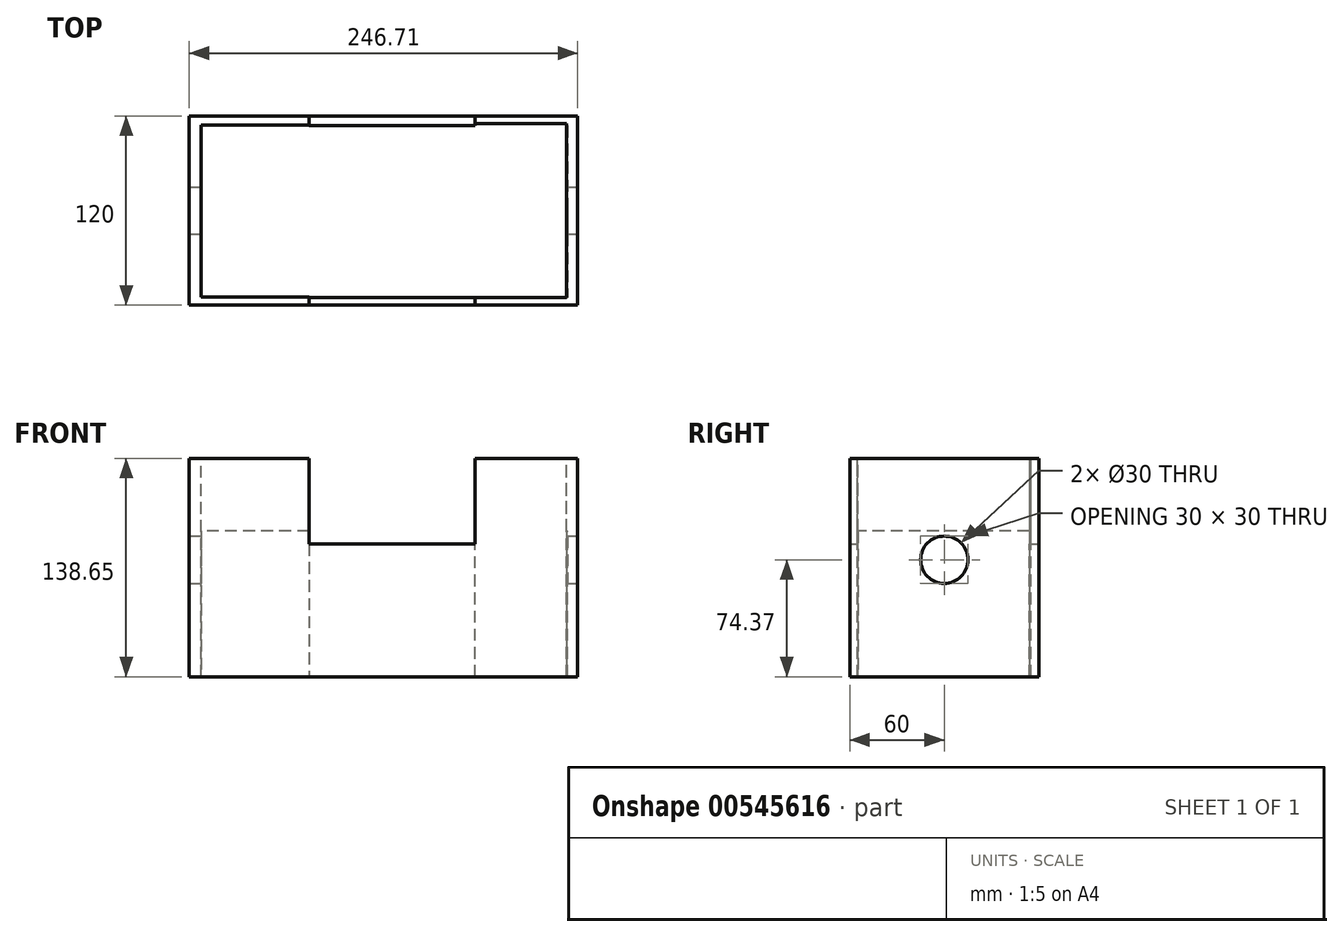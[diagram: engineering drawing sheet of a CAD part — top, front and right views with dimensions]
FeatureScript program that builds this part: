
annotation { "Feature Type Name" : "Feature", "Feature Type Description" : "" }
export const myFeature = defineFeature(function(context is Context, id is Id, definition is map)
    precondition{}
    {
        {
            var Q0;
            Q0=qCreatedBy(makeId("Front.planeOp"),FACE);
            var sketch = newSketch(context, id + "F0", { "sketchPlane" : qUnion([Q0])});
            skLineSegment(sketch, "E0.top", {"start": v(-117.19, -92.62) * mm, "end": v(129.52, -92.62) * mm});
            skLineSegment(sketch, "E0.left", {"start": v(-117.19, 46.03) * mm, "end": v(-117.19, -92.62) * mm});
            skLineSegment(sketch, "E0.right", {"start": v(129.52, 46.03) * mm, "end": v(129.52, -92.62) * mm});
            skLineSegment(sketch, "E1", {"start": v(-117.19, 46.03) * mm, "end": v(-41.02, 46.03) * mm});
            skLineSegment(sketch, "E2", {"start": v(-41.02, 46.03) * mm, "end": v(-41.02, -8.22) * mm});
            skLineSegment(sketch, "E3", {"start": v(-41.02, -8.22) * mm, "end": v(64.28, -8.22) * mm});
            skLineSegment(sketch, "E4", {"start": v(64.28, -8.22) * mm, "end": v(64.28, 46.03) * mm});
            skLineSegment(sketch, "E5", {"start": v(64.28, 46.03) * mm, "end": v(129.52, 46.03) * mm});
            skSolve(sketch);
        }
        {
            var Q0;
            Q0 = qSketchRegion(id + "F0", true);
            extrude(context, id + "F1", {"entities" : qUnion([Q0]), "depth" : 120 * mm, "offsetDistance" : 25 * mm, "symmetric" : true});
        }
        {
            var Q0;
            Q0=qCreatedBy(makeId("Top.planeOp"),FACE);
            var sketch = newSketch(context, id + "F2", { "sketchPlane" : qUnion([Q0])});
            skLineSegment(sketch, "E6.bottom", {"start": v(-109.67, 53.98) * mm, "end": v(123.15, 53.98) * mm});
            skLineSegment(sketch, "E6.top", {"start": v(-109.67, -55.13) * mm, "end": v(123.15, -55.13) * mm});
            skLineSegment(sketch, "E6.left", {"start": v(-109.67, 53.98) * mm, "end": v(-109.67, -55.13) * mm});
            skLineSegment(sketch, "E6.right", {"start": v(123.15, 53.98) * mm, "end": v(123.15, -55.13) * mm});
            skSolve(sketch);
        }
        {
            var Q0;
            Q0=makeQuery(id+"F1.opExtrude","SWEPT_FACE",FACE,{"disambiguationData":[OSD([sQuery(id+"F0.wireOp",EDGE,"E0.right")])]});
            var sketch = newSketch(context, id + "F3", { "sketchPlane" : qUnion([Q0])});
            skCircle(sketch, "E7", {"center": v(0, -18.25) * mm, "radius": 17.73 * mm});
            skSolve(sketch);
        }
        {
            var Q0;
            Q0=makeQuery(id+"F1.opExtrude","SWEPT_FACE",FACE,{"disambiguationData":[OSD([sQuery(id+"F0.wireOp",EDGE,"E1")])]});
            var sketch = newSketch(context, id + "F4", { "sketchPlane" : qUnion([Q0])});
            skLineSegment(sketch, "E8.bottom", {"start": v(-109.75, 54.3) * mm, "end": v(-41.02, 54.3) * mm});
            skLineSegment(sketch, "E8.top", {"start": v(-109.75, -54.85) * mm, "end": v(-41.02, -54.85) * mm});
            skLineSegment(sketch, "E8.left", {"start": v(-109.75, 54.3) * mm, "end": v(-109.75, -54.85) * mm});
            skLineSegment(sketch, "E8.right", {"start": v(-41.02, 54.3) * mm, "end": v(-41.02, -54.85) * mm});
            skSolve(sketch);
        }
        {
            var Q0;
            Q0=makeQuery(id+"F4.imprint","IMPRINT",FACE,{"disambiguationData":[TD([[makeQuery(id+"F4.imprint","IMPRINT",EDGE,{"derivedFrom":sQuery(id+"F4.wireOp",EDGE,"E8.bottom")}),-1.0]])]});
            extrude(context, id + "F5", {"entities" : qUnion([Q0]), "operationType" : NewBodyOperationType.REMOVE, "oppositeDirection" : true, "depth" : 150.7 * mm, "offsetDistance" : 25 * mm});
        }
        {
            var Q0;
            Q0=makeQuery(id+"F2.imprint","IMPRINT",FACE,{"disambiguationData":[TD([[makeQuery(id+"F2.imprint","IMPRINT",EDGE,{"derivedFrom":sQuery(id+"F2.wireOp",EDGE,"E6.bottom")}),-1.0]])]});
            extrude(context, id + "F6", {"entities" : qUnion([Q0]), "operationType" : NewBodyOperationType.REMOVE, "oppositeDirection" : true, "depth" : 101.1 * mm, "offsetDistance" : 25 * mm});
        }
        {
            var Q0;
            Q0=makeQuery(id+"F1.opExtrude","SWEPT_FACE",FACE,{"disambiguationData":[OSD([sQuery(id+"F0.wireOp",EDGE,"E5")])]});
            var sketch = newSketch(context, id + "F7", { "sketchPlane" : qUnion([Q0])});
            skLineSegment(sketch, "E9.bottom", {"start": v(64.28, 55.13) * mm, "end": v(122.36, 55.13) * mm});
            skLineSegment(sketch, "E9.top", {"start": v(64.28, -55.13) * mm, "end": v(122.36, -55.13) * mm});
            skLineSegment(sketch, "E9.left", {"start": v(64.28, 55.13) * mm, "end": v(64.28, -55.13) * mm});
            skLineSegment(sketch, "E9.right", {"start": v(122.36, 55.13) * mm, "end": v(122.36, -55.13) * mm});
            skSolve(sketch);
        }
        {
            var Q0;
            Q0=makeQuery(id+"F7.imprint","IMPRINT",FACE,{"disambiguationData":[TD([[makeQuery(id+"F7.imprint","IMPRINT",EDGE,{"derivedFrom":sQuery(id+"F7.wireOp",EDGE,"E9.bottom")}),-1.0]])]});
            extrude(context, id + "F8", {"entities" : qUnion([Q0]), "operationType" : NewBodyOperationType.REMOVE, "oppositeDirection" : true, "depth" : 147.8 * mm, "offsetDistance" : 25 * mm});
        }
        {
            var Q0;
            Q0=sQuery(id+"F3.wireOp",VERTEX,"E7.center");
            var Q1;
            Q1=makeQuery(id+"F1.opExtrude","SWEPT_BODY",BODY,{"disambiguationData":[OSD([sQuery(id+"F0.wireOp",EDGE,"E0.top"),sQuery(id+"F0.wireOp",EDGE,"E0.left"),sQuery(id+"F0.wireOp",EDGE,"E0.right"),sQuery(id+"F0.wireOp",EDGE,"E1"),sQuery(id+"F0.wireOp",EDGE,"E2"),sQuery(id+"F0.wireOp",EDGE,"E3"),sQuery(id+"F0.wireOp",EDGE,"E4"),sQuery(id+"F0.wireOp",EDGE,"E5")])]});
            hole(context, id + "F9", {"style" : HoleStyle.SIMPLE, "endStyle" : HoleEndStyle.THROUGH, "holeDiameter" : 30 * mm, "majorDiameter" : 5 * mm, "isTappedThrough" : true, "tappedDepth" : 12 * mm, "tapClearance" : 3, "locations" : qUnion([Q0]), "scope" : qUnion([Q1])});
        }
    });
